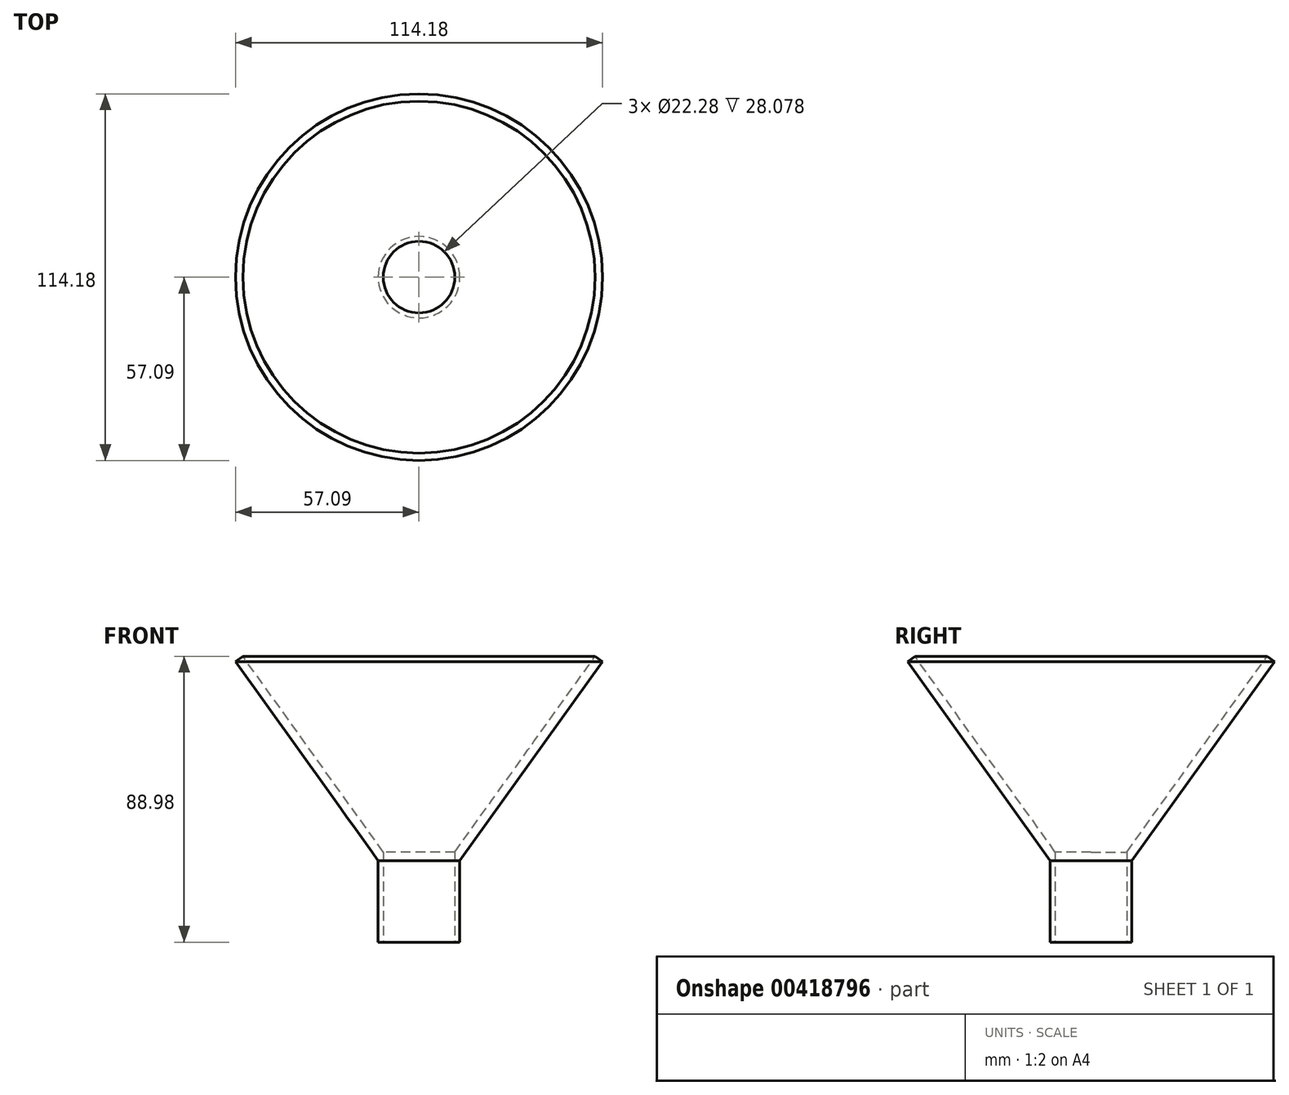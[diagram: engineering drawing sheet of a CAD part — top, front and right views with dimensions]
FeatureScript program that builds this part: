
annotation { "Feature Type Name" : "Feature", "Feature Type Description" : "" }
export const myFeature = defineFeature(function(context is Context, id is Id, definition is map)
    precondition{}
    {
        {
            var Q0;
            Q0=qCreatedBy(makeId("Front.planeOp"),FACE);
            var sketch = newSketch(context, id + "F0", { "sketchPlane" : qUnion([Q0])});
            skLineSegment(sketch, "E0", {"start": v(0, 0) * mm, "end": v(0, -25.4) * mm});
            skLineSegment(sketch, "E1", {"start": v(0, -25.4) * mm, "end": v(-12.7, -25.4) * mm});
            skLineSegment(sketch, "E2", {"start": v(-12.7, -25.4) * mm, "end": v(-12.7, 0) * mm});
            skLineSegment(sketch, "E3", {"start": v(0, 0) * mm, "end": v(44.39, 61.94) * mm});
            skLineSegment(sketch, "E4", {"start": v(44.39, 61.94) * mm, "end": v(42.09, 63.58) * mm});
            skLineSegment(sketch, "E5", {"start": v(42.09, 63.58) * mm, "end": v(-3.48, 0) * mm});
            skLineSegment(sketch, "E6", {"start": v(-3.48, 0) * mm, "end": v(0, 0) * mm});
            skLineSegment(sketch, "E7", {"start": v(-12.7, 0) * mm, "end": v(-3.48, 0) * mm});
            skSolve(sketch);
        }
        {
            var Q0;
            Q0 = qSketchRegion(id + "F0", true);
            var Q1;
            Q1=sQuery(id+"F0.wireOp",EDGE,"E2");
            revolve(context, id + "F1", {"entities" : qUnion([Q0]), "axis" : qUnion([Q1]), "revolveType" : RevolveType.FULL});
        }
        {
            var Q0;
            Q0=makeQuery(id+"F1.opRevolve","SWEPT_FACE",FACE,{"disambiguationData":[OSD([sQuery(id+"F0.wireOp",EDGE,"E1")])]});
            var sketch = newSketch(context, id + "F2", { "sketchPlane" : qUnion([Q0])});
            skCircle(sketch, "E8", {"center": v(-12.7, 0) * mm, "radius": 11.14 * mm});
            skSolve(sketch);
        }
        {
            var Q0;
            Q0 = qSketchRegion(id + "F2", true);
            extrude(context, id + "F3", {"entities" : qUnion([Q0]), "operationType" : NewBodyOperationType.REMOVE, "oppositeDirection" : true, "depth" : 50.8 * mm});
        }
    });
